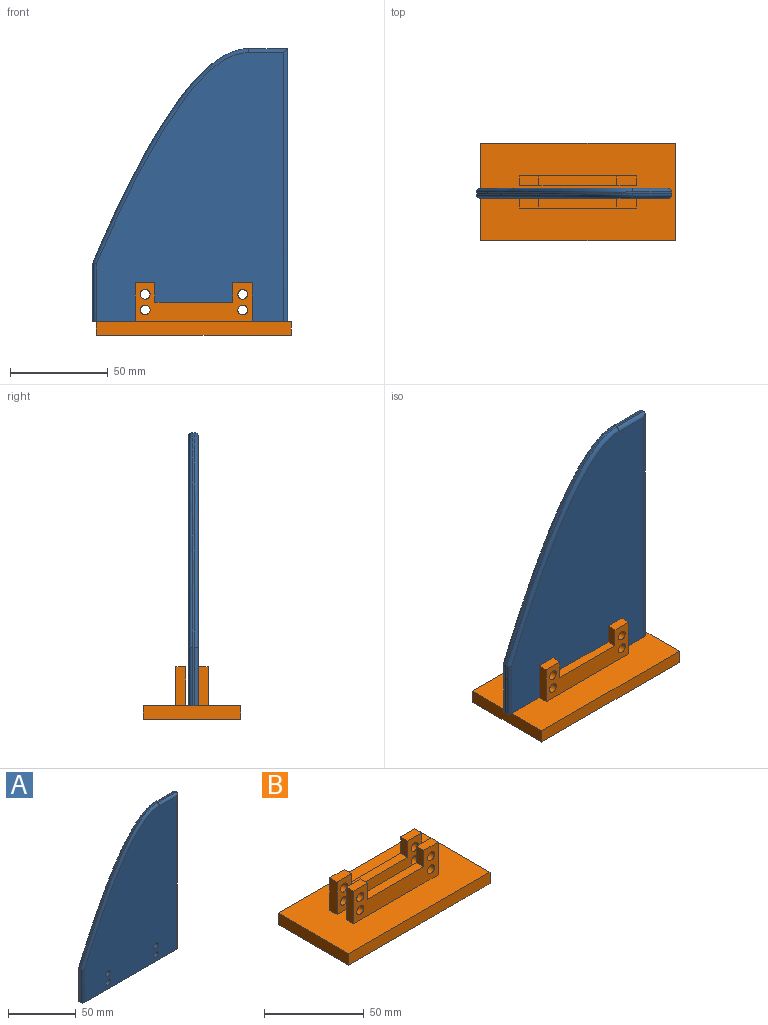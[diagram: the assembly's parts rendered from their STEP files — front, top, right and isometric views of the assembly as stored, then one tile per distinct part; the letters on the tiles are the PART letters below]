
ASSEMBLY  parts=2 mates=1
PART A: 19 faces, bbox 101x5x140 mm
  f0: plane 30x1mm, normal (-1,0,0), area 30mm2, adj f1,f4,f7,f11
  f1: plane 100x5mm, normal (0,0,-1), area 496.6mm2, adj f0,f2,f5,f6,f7,f8,f11,f12
  f2: plane 140x1mm, normal (1,0,0), area 140mm2, adj f1,f3,f8,f12
  f3: plane 20x1mm, normal (0,0,1), area 20mm2, adj f2,f4,f10,f14
  f4: extruded ~110x80mm, area 140.8mm2, adj f0,f3,f9,f13
  f5: plane 138x96.01mm, normal (0,-1,0), area 10092.5mm2, adj f1,f11,f12,f13,f14,f15,f16,f17
  f6: plane 138x96.01mm, normal (0,1,0), area 10092.5mm2, adj f1,f7,f8,f9,f10,f15,f16,f17
  f7: cylinder r=2mm len=30mm, axis (0,0,-1), area 93.6mm2, adj f0,f1,f6,f9
  f8: cylinder r=2mm len=140mm, axis (0,0,1), area 436.7mm2, adj f1,f2,f6,f10
  f9: bspline ~113.09x95.07mm, area 438.9mm2, adj f4,f6,f7,f10
  f10: cylinder r=2mm len=20mm, axis (-1,0,0), area 59.7mm2, adj f3,f6,f8,f9
  f11: cylinder r=2mm len=30mm, axis (0,0,1), area 93.6mm2, adj f0,f1,f5,f13
  f12: cylinder r=2mm len=140mm, axis (0,0,-1), area 436.7mm2, adj f1,f2,f5,f14
  f13: bspline ~113.09x95.07mm, area 438.9mm2, adj f4,f5,f11,f14
  f14: cylinder r=2mm len=20mm, axis (1,0,0), area 59.7mm2, adj f3,f5,f12,f13
  f15: cylinder r=2.5mm len=5mm, axis (0,-1,0), area 78.5mm2, adj f5,f6
  f16: cylinder r=2.5mm len=5mm, axis (0,-1,0), area 78.5mm2, adj f5,f6
  f17: cylinder r=2.5mm len=5mm, axis (0,-1,0), area 78.5mm2, adj f5,f6
  f18: cylinder r=2.5mm len=5mm, axis (0,-1,0), area 78.5mm2, adj f5,f6
PART B: 32 faces, bbox 100x50x27 mm
  f0: plane 100x50mm, normal (0,0,1), area 4400mm2, adj f1,f3,f4,f5,f6,f7,f8,f11
  f1: plane 50x7mm, normal (-1,0,0), area 350mm2, adj f0,f2,f4,f5
  f2: plane 100x50mm, normal (0,0,-1), area 5000mm2, adj f1,f3,f4,f5
  f3: plane 50x7mm, normal (1,0,0), area 350mm2, adj f0,f2,f4,f5
  f4: plane 100x7mm, normal (0,-1,0), area 700mm2, adj f0,f1,f2,f3
  f5: plane 100x7mm, normal (0,1,0), area 700mm2, adj f0,f1,f2,f3
  f6: plane 60x20mm, normal (0,1,0), area 721.5mm2, adj f0,f7,f9,f10,f11,f12,f13,f22
  f7: plane 20x5mm, normal (-1,0,0), area 100mm2, adj f0,f6,f8,f10
  f8: plane 60x20mm, normal (0,-1,0), area 721.5mm2, adj f0,f7,f9,f10,f11,f12,f13,f22
  f9: plane 10x5mm, normal (1,0,0), area 50mm2, adj f6,f8,f10,f22
  f10: plane 10x5mm, normal (0,0,1), area 50mm2, adj f6,f7,f8,f9
  f11: plane 20x5mm, normal (1,0,0), area 100mm2, adj f0,f6,f8,f13
  f12: plane 10x5mm, normal (-1,0,0), area 50mm2, adj f6,f8,f13,f22
  f13: plane 10x5mm, normal (0,0,1), area 50mm2, adj f6,f8,f11,f12
  f14: plane 60x20mm, normal (0,1,0), area 721.5mm2, adj f0,f15,f17,f18,f19,f20,f21,f23
  f15: plane 20x5mm, normal (-1,0,0), area 100mm2, adj f0,f14,f16,f18
  f16: plane 60x20mm, normal (0,-1,0), area 721.5mm2, adj f0,f15,f17,f18,f19,f20,f21,f23
  f17: plane 10x5mm, normal (1,0,0), area 50mm2, adj f14,f16,f18,f23
  f18: plane 10x5mm, normal (0,0,1), area 50mm2, adj f14,f15,f16,f17
  f19: plane 20x5mm, normal (1,0,0), area 100mm2, adj f0,f14,f16,f21
  f20: plane 10x5mm, normal (-1,0,0), area 50mm2, adj f14,f16,f21,f23
  f21: plane 10x5mm, normal (0,0,1), area 50mm2, adj f14,f16,f19,f20
  f22: plane 40x5mm, normal (0,0,1), area 200mm2, adj f6,f8,f9,f12
  f23: plane 40x5mm, normal (0,0,1), area 200mm2, adj f14,f16,f17,f20
  f24: cylinder r=2.5mm len=5mm, axis (0,-1,0), area 78.5mm2, adj f14,f16
  f25: cylinder r=2.5mm len=5mm, axis (0,-1,0), area 78.5mm2, adj f14,f16
  f26: cylinder r=2.5mm len=5mm, axis (0,-1,0), area 78.5mm2, adj f14,f16
  f27: cylinder r=2.5mm len=5mm, axis (0,-1,0), area 78.5mm2, adj f14,f16
  f28: cylinder r=2.5mm len=5mm, axis (0,-1,0), area 78.5mm2, adj f6,f8
  f29: cylinder r=2.5mm len=5mm, axis (0,-1,0), area 78.5mm2, adj f6,f8
  f30: cylinder r=2.5mm len=5mm, axis (0,-1,0), area 78.5mm2, adj f6,f8
  f31: cylinder r=2.5mm len=5mm, axis (0,-1,0), area 78.5mm2, adj f6,f8
PLACE A t=(-6.58,8.3,19.76)mm
PLACE B t=(-3.31,31.55,-22.94)mm
MATE fastened A.f16 <-> B.f24  axis (0,-1,0) through (-9.33,3.3,3.76)mm
